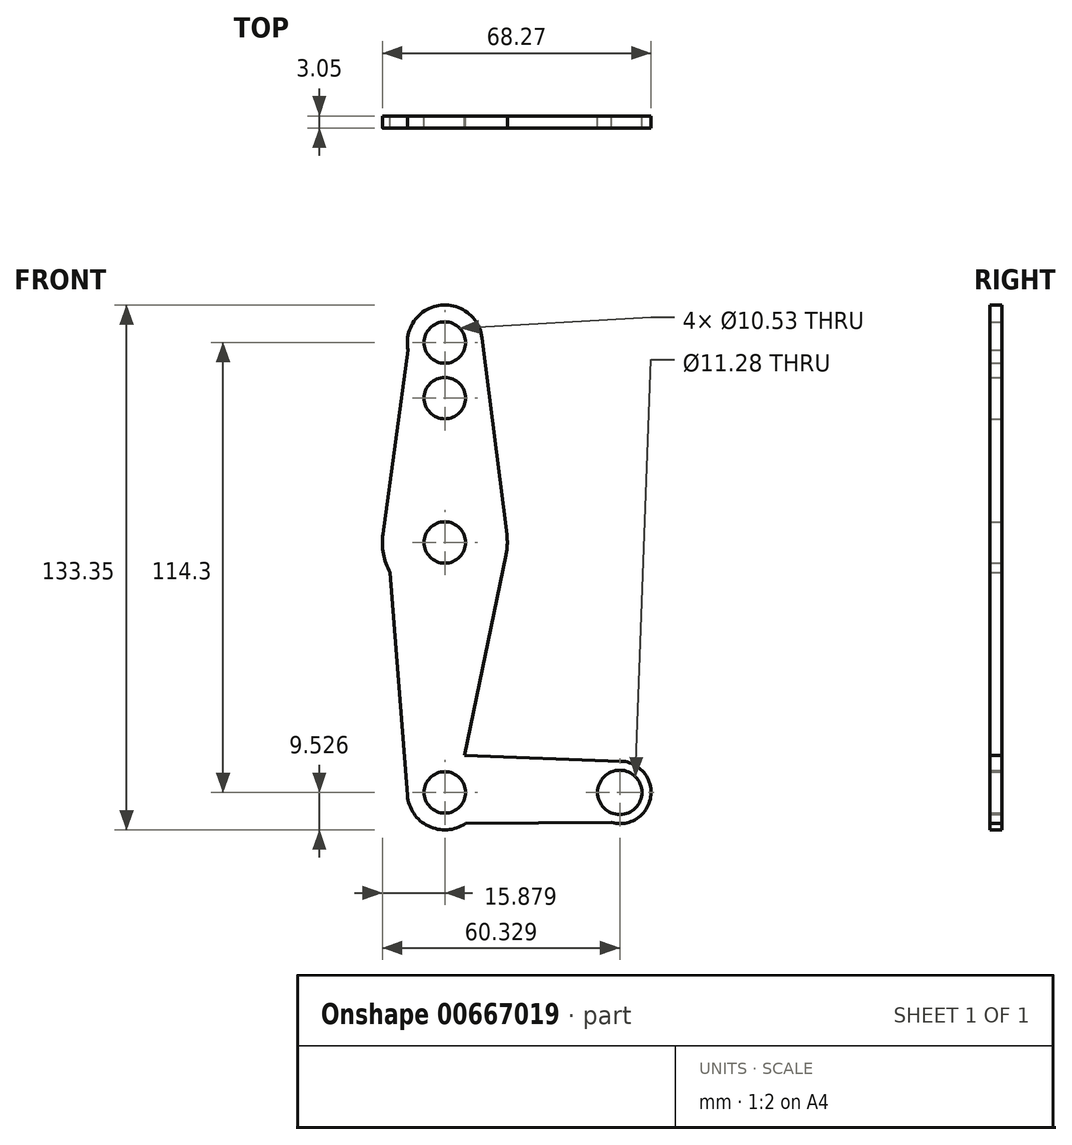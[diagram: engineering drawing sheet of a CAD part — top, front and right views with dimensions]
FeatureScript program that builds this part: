
annotation { "Feature Type Name" : "Feature", "Feature Type Description" : "" }
export const myFeature = defineFeature(function(context is Context, id is Id, definition is map)
    precondition{}
    {
        {
            var Q0;
            Q0=qCreatedBy(makeId("Front.planeOp"),FACE);
            var sketch = newSketch(context, id + "F0", { "sketchPlane" : qUnion([Q0])});
            skLineSegment(sketch, "E0", {"start": v(-32.78, 71.23) * mm, "end": v(-32.78, -43.07) * mm});
            skLineSegment(sketch, "E1", {"start": v(-32.78, -43.07) * mm, "end": v(11.67, -43.07) * mm});
            skCircle(sketch, "E2", {"center": v(-32.78, 71.23) * mm, "radius": 9.53 * mm});
            skCircle(sketch, "E3", {"center": v(-32.78, 20.43) * mm, "radius": 15.88 * mm});
            skCircle(sketch, "E4", {"center": v(-32.78, -43.07) * mm, "radius": 9.53 * mm});
            skCircle(sketch, "E5", {"center": v(11.67, -43.07) * mm, "radius": 7.94 * mm});
            skLineSegment(sketch, "E6", {"start": v(-27.52, -64.9) * mm, "end": v(-27.52, -71.76) * mm});
            skPoint(sketch, "E7.endSnap0", {"position": v(-27.52, -71.76) * mm});
            skPoint(sketch, "E8.start.orphan", {"position": v(11.67, -92.67) * mm});
            skPoint(sketch, "E9.orphan", {"position": v(45.58, -78.64) * mm});
            skPoint(sketch, "E10.orphan", {"position": v(-27.52, -51.01) * mm});
            skPoint(sketch, "E11.orphan", {"position": v(-27.52, -78.64) * mm});
            skPoint(sketch, "E12.end.orphan", {"position": v(0, 67.7) * mm});
            skPoint(sketch, "E12.start.orphan", {"position": v(-10.56, -43.07) * mm});
            skLineSegment(sketch, "E13", {"start": v(-23.33, 72.42) * mm, "end": v(-17.03, 22.41) * mm});
            skLineSegment(sketch, "E14", {"start": v(-17.23, 17.22) * mm, "end": v(-27.96, -34.86) * mm});
            skLineSegment(sketch, "E15", {"start": v(-27.52, -51.01) * mm, "end": v(9.62, -50.74) * mm});
            skCircle(sketch, "E16", {"center": v(-32.78, 71.23) * mm, "radius": 5.27 * mm});
            skArc(sketch, "E17", {"start": v(-37.76, 55.38) * mm, "mid": v(-37.43, 57.1) * mm, "end": v(-37.76, 58.83) * mm});
            skCircle(sketch, "E18", {"center": v(-32.78, 57.1) * mm, "radius": 5.27 * mm});
            skCircle(sketch, "E19", {"center": v(-32.78, 20.43) * mm, "radius": 5.27 * mm});
            skCircle(sketch, "E20", {"center": v(-32.78, -43.07) * mm, "radius": 5.27 * mm});
            skCircle(sketch, "E21", {"center": v(11.67, -43.07) * mm, "radius": 5.64 * mm});
            skLineSegment(sketch, "E22", {"start": v(11.95, -35.14) * mm, "end": v(-32.44, -33.56) * mm});
            skLineSegment(sketch, "E23", {"start": v(-46.69, 12.77) * mm, "end": v(-42.28, -43.81) * mm});
            skPoint(sketch, "E24.end.orphan", {"position": v(-42.12, 73.11) * mm});
            skLineSegment(sketch, "E25", {"start": v(-42.12, 69.34) * mm, "end": v(-48.5, 22.58) * mm});
            skSolve(sketch);
        }
        {
            var Q0;
            Q0 = qSketchRegion(id + "F0", true);
            var Q1;
            {var subQ0=sQuery(id+"F0.wireOp",EDGE,"E3");var subQ1=sQuery(id+"F0.wireOp",EDGE,"E0");var subQ2=makeQuery(id+"F0.imprint","INTERSECT",VERTEX,{"disambiguationData":[OD(0.0)],"derivedFrom":[subQ1,subQ0]});Q1=makeQuery(id+"F0.imprint","IMPRINT",FACE,{"disambiguationData":[TD([[makeQuery(id+"F0.imprint","IMPRINT",EDGE,{"disambiguationData":[TD([[subQ2,-1.0]])],"derivedFrom":subQ1}),-1.0]])]});}
            var Q2;
            {var subQ0=sQuery(id+"F0.wireOp",EDGE,"E4");var subQ4=sQuery(id+"F0.wireOp",EDGE,"E0");var subQ9=makeQuery(id+"F0.imprint","INTERSECT",VERTEX,{"derivedFrom":[subQ4,subQ0]});Q2=makeQuery(id+"F0.imprint","IMPRINT",FACE,{"disambiguationData":[TD([[makeQuery(id+"F0.imprint","IMPRINT",EDGE,{"disambiguationData":[TD([[subQ9,-1.0]])],"derivedFrom":subQ4}),1.0]])]});}
            extrude(context, id + "F1", {"entities" : qUnion([Q0, Q1, Q2]), "depth" : 3.05 * mm, "offsetDistance" : 25.4 * mm});
        }
    });
